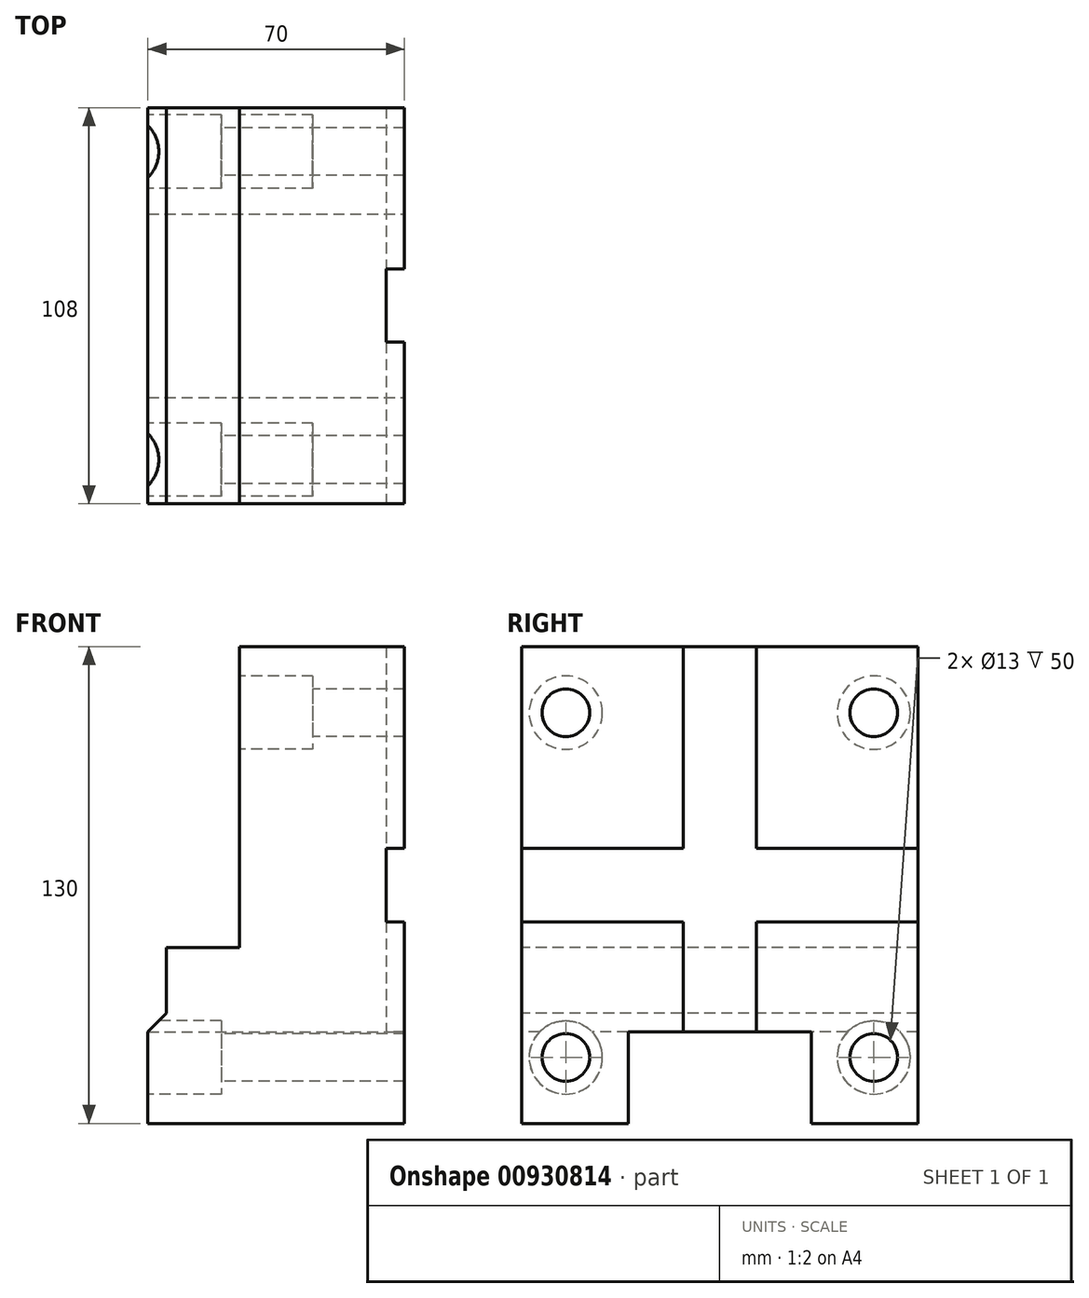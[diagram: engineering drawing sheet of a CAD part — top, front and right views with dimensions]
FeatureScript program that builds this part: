
annotation { "Feature Type Name" : "Feature", "Feature Type Description" : "" }
export const myFeature = defineFeature(function(context is Context, id is Id, definition is map)
    precondition{}
    {
        {
            var Q0;
            Q0=qCreatedBy(makeId("Right.planeOp"),FACE);
            var sketch = newSketch(context, id + "F0", { "sketchPlane" : qUnion([Q0])});
            skLineSegment(sketch, "E0.bottom", {"start": v(54, 65) * mm, "end": v(-54, 65) * mm});
            skLineSegment(sketch, "E0.top", {"start": v(54, -65) * mm, "end": v(-54, -65) * mm});
            skLineSegment(sketch, "E0.left", {"start": v(54, 65) * mm, "end": v(54, -65) * mm});
            skLineSegment(sketch, "E0.right", {"start": v(-54, 65) * mm, "end": v(-54, -65) * mm});
            skPoint(sketch, "E0.middle", {"position": v(0, 0) * mm});
            skSolve(sketch);
        }
        {
            var Q0;
            Q0 = qSketchRegion(id + "F0", true);
            extrude(context, id + "F1", {"entities" : qUnion([Q0]), "oppositeDirection" : true, "depth" : 70 * mm, "offsetDistance" : 25 * mm});
        }
        {
            var Q0;
            Q0=makeQuery(id+"F1.opExtrude","CAP_FACE",FACE,{"disambiguationData":[OSD([sQuery(id+"F0.wireOp",EDGE,"E0.bottom"),sQuery(id+"F0.wireOp",EDGE,"E0.top"),sQuery(id+"F0.wireOp",EDGE,"E0.left"),sQuery(id+"F0.wireOp",EDGE,"E0.right")])],"isStart":false});
            var sketch = newSketch(context, id + "F2", { "sketchPlane" : qUnion([Q0])});
            skCircle(sketch, "E1", {"center": v(-42, 47) * mm, "radius": 6.5 * mm});
            skCircle(sketch, "E2.MirrorC", {"center": v(42, 47) * mm, "radius": 6.5 * mm});
            skCircle(sketch, "E3.MirrorC", {"center": v(-42, -47) * mm, "radius": 6.5 * mm});
            skCircle(sketch, "E4.MirrorC", {"center": v(42, -47) * mm, "radius": 6.5 * mm});
            skSolve(sketch);
        }
        {
            var Q0;
            Q0 = qSketchRegion(id + "F2", true);
            extrude(context, id + "F3", {"entities" : qUnion([Q0]), "operationType" : NewBodyOperationType.REMOVE, "endBound" : BoundingType.THROUGH_ALL, "oppositeDirection" : true, "depth" : 25 * mm, "offsetDistance" : 25 * mm});
        }
        {
            var Q0;
            Q0=makeQuery(id+"F1.opExtrude","SWEPT_FACE",FACE,{"disambiguationData":[OSD([sQuery(id+"F0.wireOp",EDGE,"E0.top")])]});
            var sketch = newSketch(context, id + "F4", { "sketchPlane" : qUnion([Q0])});
            skLineSegment(sketch, "E5.bottom", {"start": v(-70, 25) * mm, "end": v(0, 25) * mm});
            skLineSegment(sketch, "E5.top", {"start": v(-70, -25) * mm, "end": v(0, -25) * mm});
            skLineSegment(sketch, "E5.left", {"start": v(-70, 25) * mm, "end": v(-70, -25) * mm});
            skLineSegment(sketch, "E5.right", {"start": v(0, 25) * mm, "end": v(0, -25) * mm});
            skPoint(sketch, "E5.middle", {"position": v(-35, 0) * mm});
            skSolve(sketch);
        }
        {
            var Q0;
            Q0 = qSketchRegion(id + "F4", true);
            extrude(context, id + "F5", {"entities" : qUnion([Q0]), "operationType" : NewBodyOperationType.REMOVE, "oppositeDirection" : true, "depth" : 25 * mm, "offsetDistance" : 25 * mm});
        }
        {
            var Q0;
            Q0=makeQuery(id+"F1.opExtrude","CAP_FACE",FACE,{"disambiguationData":[OSD([sQuery(id+"F0.wireOp",EDGE,"E0.bottom"),sQuery(id+"F0.wireOp",EDGE,"E0.top"),sQuery(id+"F0.wireOp",EDGE,"E0.left"),sQuery(id+"F0.wireOp",EDGE,"E0.right")])],"isStart":false});
            var sketch = newSketch(context, id + "F6", { "sketchPlane" : qUnion([Q0])});
            skLineSegment(sketch, "E6.bottom", {"start": v(-54, 65) * mm, "end": v(54, 65) * mm});
            skLineSegment(sketch, "E6.top", {"start": v(-54, -17) * mm, "end": v(54, -17) * mm});
            skLineSegment(sketch, "E6.left", {"start": v(-54, 65) * mm, "end": v(-54, -17) * mm});
            skLineSegment(sketch, "E6.right", {"start": v(54, 65) * mm, "end": v(54, -17) * mm});
            skSolve(sketch);
        }
        {
            var Q0;
            Q0 = qSketchRegion(id + "F6", true);
            extrude(context, id + "F7", {"entities" : qUnion([Q0]), "operationType" : NewBodyOperationType.REMOVE, "oppositeDirection" : true, "depth" : 25 * mm, "offsetDistance" : 25 * mm});
        }
        {
            var Q0;
            Q0=makeQuery(id+"F1.opExtrude","SWEPT_FACE",FACE,{"disambiguationData":[OSD([sQuery(id+"F0.wireOp",EDGE,"E0.right")])]});
            var sketch = newSketch(context, id + "F8", { "sketchPlane" : qUnion([Q0])});
            skLineSegment(sketch, "E7", {"start": v(-45, -17) * mm, "end": v(-65, -17) * mm});
            skLineSegment(sketch, "E8", {"start": v(-65, -17) * mm, "end": v(-65, -35) * mm});
            skLineSegment(sketch, "E9", {"start": v(-65, -35) * mm, "end": v(-70, -40) * mm});
            skLineSegment(sketch, "E10", {"start": v(-70, -40) * mm, "end": v(-70, -65) * mm});
            skSolve(sketch);
        }
        {
            var Q0;
            {var subQ0=sQuery(id+"F8.wireOp",EDGE,"E8");Q0=makeQuery(id+"F8.imprint","IMPRINT",FACE,{"disambiguationData":[TD([[makeQuery(id+"F8.imprint","IMPRINT",EDGE,{"derivedFrom":subQ0}),-1.0]])]});}
            extrude(context, id + "F9", {"entities" : qUnion([Q0]), "operationType" : NewBodyOperationType.REMOVE, "endBound" : BoundingType.THROUGH_ALL, "oppositeDirection" : true, "depth" : 25 * mm, "offsetDistance" : 25 * mm});
        }
        {
            var Q0;
            {var subQ1=sQuery(id+"F0.wireOp",EDGE,"E0.left");var subQ2=sQuery(id+"F0.wireOp",EDGE,"E0.top");Q0=makeQuery(id+"F9.boolean.opBoolean","SPLIT",FACE,{"disambiguationData":[TD([makeQuery(id+"F1.opExtrude","SWEPT_FACE",FACE,{"disambiguationData":[OSD([subQ1])]})])],"derivedFrom":makeQuery(id+"F1.opExtrude","CAP_FACE",FACE,{"disambiguationData":[OSD([sQuery(id+"F0.wireOp",EDGE,"E0.bottom"),subQ2,subQ1,sQuery(id+"F0.wireOp",EDGE,"E0.right")])],"isStart":false})});}
            var sketch = newSketch(context, id + "F10", { "sketchPlane" : qUnion([Q0])});
            skCircle(sketch, "E11", {"center": v(-42, -47) * mm, "radius": 10 * mm});
            skCircle(sketch, "E12.MirrorC", {"center": v(42, -47) * mm, "radius": 10 * mm});
            skSolve(sketch);
        }
        {
            var Q0;
            Q0 = qSketchRegion(id + "F10", true);
            extrude(context, id + "F11", {"entities" : qUnion([Q0]), "operationType" : NewBodyOperationType.REMOVE, "oppositeDirection" : true, "depth" : 20 * mm, "offsetDistance" : 25 * mm});
        }
        {
            var Q0;
            Q0=makeQuery(id+"F7.boolean.opBoolean","COPY",FACE,{"derivedFrom":makeQuery(id+"F7.opExtrude","CAP_FACE",FACE,{"disambiguationData":[OSD([sQuery(id+"F6.wireOp",EDGE,"E6.bottom"),sQuery(id+"F6.wireOp",EDGE,"E6.top"),sQuery(id+"F6.wireOp",EDGE,"E6.left"),sQuery(id+"F6.wireOp",EDGE,"E6.right")])],"isStart":false})});
            var sketch = newSketch(context, id + "F12", { "sketchPlane" : qUnion([Q0])});
            skCircle(sketch, "E13", {"center": v(-42, 47) * mm, "radius": 10 * mm});
            skCircle(sketch, "E14.MirrorC", {"center": v(42, 47) * mm, "radius": 10 * mm});
            skSolve(sketch);
        }
        {
            var Q0;
            Q0 = qSketchRegion(id + "F12", true);
            extrude(context, id + "F13", {"entities" : qUnion([Q0]), "operationType" : NewBodyOperationType.REMOVE, "oppositeDirection" : true, "depth" : 20 * mm, "offsetDistance" : 25 * mm});
        }
        {
            var Q0;
            Q0=makeQuery(id+"F1.opExtrude","CAP_FACE",FACE,{"disambiguationData":[OSD([sQuery(id+"F0.wireOp",EDGE,"E0.bottom"),sQuery(id+"F0.wireOp",EDGE,"E0.top"),sQuery(id+"F0.wireOp",EDGE,"E0.left"),sQuery(id+"F0.wireOp",EDGE,"E0.right")])],"isStart":true});
            var sketch = newSketch(context, id + "F14", { "sketchPlane" : qUnion([Q0])});
            skLineSegment(sketch, "E15.bottom", {"start": v(54, 10) * mm, "end": v(-54, 10) * mm});
            skLineSegment(sketch, "E15.top", {"start": v(54, -10) * mm, "end": v(-54, -10) * mm});
            skLineSegment(sketch, "E15.left", {"start": v(54, 10) * mm, "end": v(54, -10) * mm});
            skLineSegment(sketch, "E15.right", {"start": v(-54, 10) * mm, "end": v(-54, -10) * mm});
            skPoint(sketch, "E15.middle", {"position": v(0, 0) * mm});
            skLineSegment(sketch, "E16.bottom", {"start": v(-10, 65) * mm, "end": v(10, 65) * mm});
            skLineSegment(sketch, "E16.top", {"start": v(-10, -65) * mm, "end": v(10, -65) * mm});
            skLineSegment(sketch, "E16.left", {"start": v(-10, 65) * mm, "end": v(-10, -65) * mm});
            skLineSegment(sketch, "E16.right", {"start": v(10, 65) * mm, "end": v(10, -65) * mm});
            skSolve(sketch);
        }
        {
            var Q0;
            Q0 = qSketchRegion(id + "F14", true);
            extrude(context, id + "F15", {"entities" : qUnion([Q0]), "operationType" : NewBodyOperationType.REMOVE, "oppositeDirection" : true, "depth" : 5 * mm, "offsetDistance" : 25 * mm});
        }
    });
